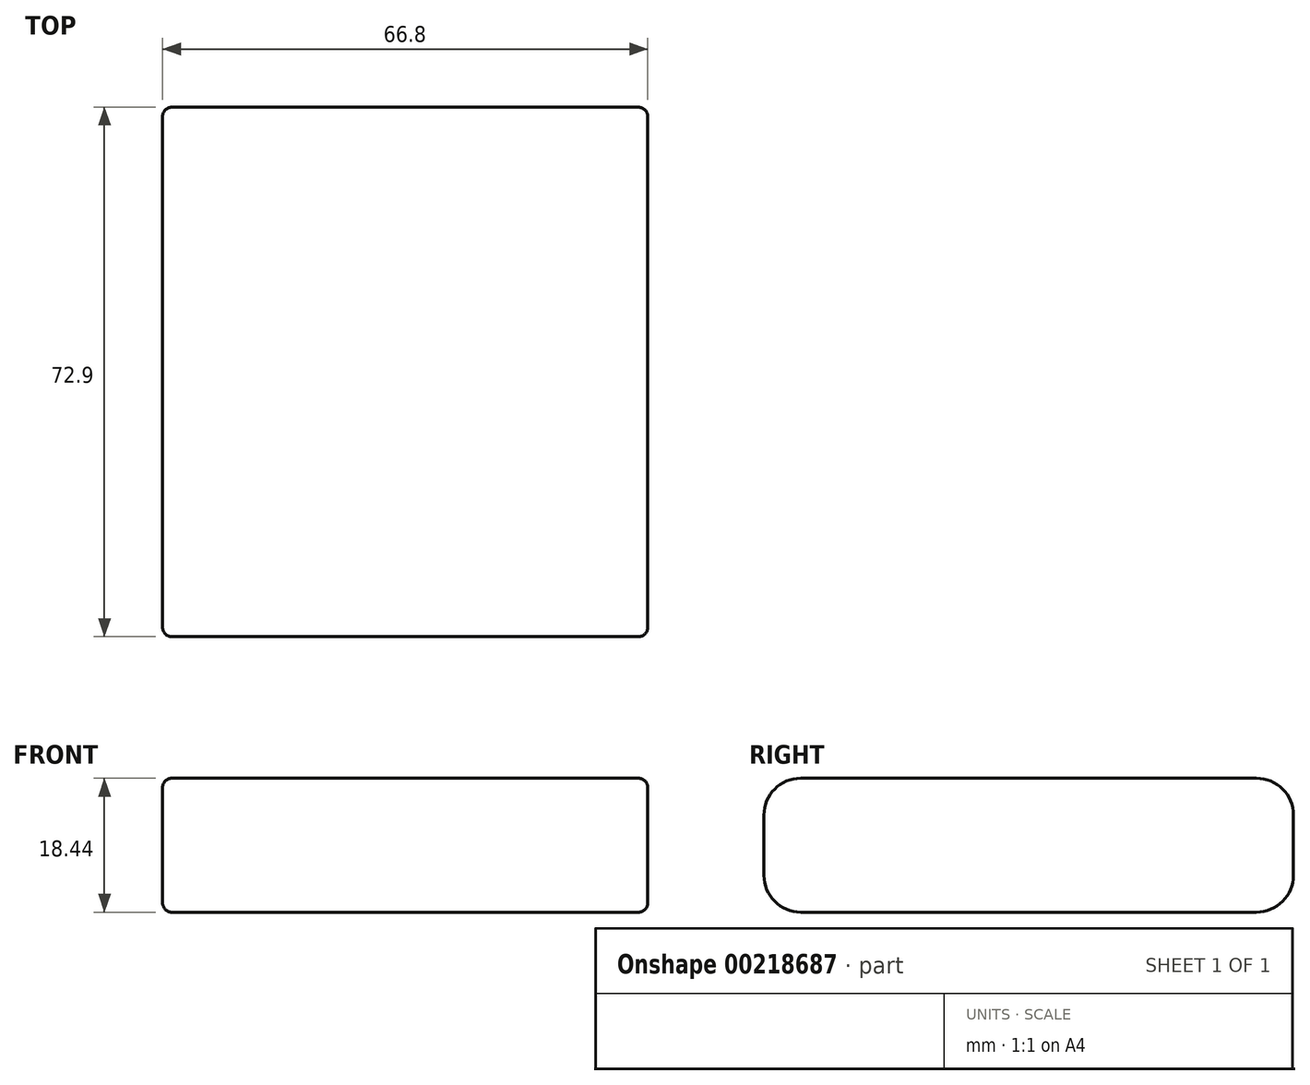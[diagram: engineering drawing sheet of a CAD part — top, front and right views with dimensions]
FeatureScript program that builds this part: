
annotation { "Feature Type Name" : "Feature", "Feature Type Description" : "" }
export const myFeature = defineFeature(function(context is Context, id is Id, definition is map)
    precondition{}
    {
        {
            var Q0;
            Q0=qCreatedBy(makeId("Top.planeOp"),FACE);
            var sketch = newSketch(context, id + "F0", { "sketchPlane" : qUnion([Q0])});
            skLineSegment(sketch, "E0.bottom", {"start": v(-33.4, 36.45) * mm, "end": v(33.4, 36.45) * mm});
            skLineSegment(sketch, "E0.top", {"start": v(-33.4, -36.45) * mm, "end": v(33.4, -36.45) * mm});
            skLineSegment(sketch, "E0.left", {"start": v(-33.4, 36.45) * mm, "end": v(-33.4, -36.45) * mm});
            skLineSegment(sketch, "E0.right", {"start": v(33.4, 36.45) * mm, "end": v(33.4, -36.45) * mm});
            skLineSegment(sketch, "E1", {"start": v(0, 36.45) * mm, "end": v(0, -36.45) * mm, "construction": true});
            skLineSegment(sketch, "E2", {"start": v(-33.4, 0) * mm, "end": v(33.4, 0) * mm, "construction": true});
            skSolve(sketch);
        }
        {
            var Q0;
            Q0 = qSketchRegion(id + "F0", true);
            extrude(context, id + "F1", {"entities" : qUnion([Q0]), "depth" : 18.44 * mm});
        }
        {
            var Q0;
            Q0=makeQuery(id+"F1.opExtrude","CAP_EDGE",EDGE,{"disambiguationData":[OSD([sQuery(id+"F0.wireOp",EDGE,"E0.bottom")])],"isStart":false});
            var Q1;
            Q1=makeQuery(id+"F1.opExtrude","CAP_EDGE",EDGE,{"disambiguationData":[OSD([sQuery(id+"F0.wireOp",EDGE,"E0.bottom")])],"isStart":true});
            var Q2;
            Q2=makeQuery(id+"F1.opExtrude","CAP_EDGE",EDGE,{"disambiguationData":[OSD([sQuery(id+"F0.wireOp",EDGE,"E0.top")])],"isStart":false});
            var Q3;
            Q3=makeQuery(id+"F1.opExtrude","CAP_EDGE",EDGE,{"disambiguationData":[OSD([sQuery(id+"F0.wireOp",EDGE,"E0.top")])],"isStart":true});
            fillet(context, id + "F2", {"entities" : qUnion([Q0, Q1, Q2, Q3]), "radius" : 5.08 * mm, "tangentPropagation" : true, "allowEdgeOverflow" : false});
        }
        {
            var Q0;
            Q0=makeQuery(id+"F1.opExtrude","SWEPT_FACE",FACE,{"disambiguationData":[OSD([sQuery(id+"F0.wireOp",EDGE,"E0.left")])]});
            var Q1;
            Q1=makeQuery(id+"F1.opExtrude","SWEPT_FACE",FACE,{"disambiguationData":[OSD([sQuery(id+"F0.wireOp",EDGE,"E0.right")])]});
            fillet(context, id + "F3", {"entities" : qUnion([Q0, Q1]), "radius" : 1.27 * mm, "tangentPropagation" : true, "allowEdgeOverflow" : false});
        }
    });
